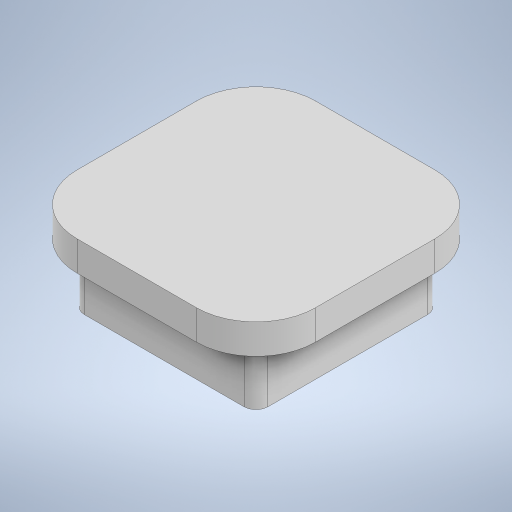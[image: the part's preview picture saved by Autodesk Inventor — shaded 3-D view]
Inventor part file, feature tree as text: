
AUTODESK INVENTOR PART (.ipt)
format: ipt  version: 2023 (Build 270158000, 158)  size: 2,161,664 bytes
history: native  units: in
note: dims shown in document units (in); Inventor stores cm internally (conversion verified against a paired STEP export)
features: extrude x8, other x7, plane x4, sketch x4, projected_geometry x3, fillet x2, chamfer x1
ambient origin geometry x8: Origin, YZ Plane, XZ Plane, XY Plane, X Axis, Y Axis, Z Axis, Center Point
bodies: Solid1 (feature_tree), Solid7 (feature_tree), Solid8 (feature_tree), Solid9 (feature_tree), Solid10 (feature_tree)
feature tree (29):
  plane  "Work Plane1"
  sketch  "Sketch3"  dims[d11=0.0118in d15=0.1969in d16=0.0in]
  extrude  "Extrusion3"  Depth=0.1969in TaperAngle=0.0deg
  extrude  "Extrusion5"  Depth=1.5748in
  extrude  "Extrusion6"  Depth=0.3937in TaperAngle=0.0deg
  plane  "Work Plane2"
  sketch  "Sketch4"  dims[d19=0.1417in d20=0.0in d21=1.5748in]
  extrude  "Extrusion7"  Depth=0.0197in TaperAngle=0.0deg
  extrude  "Extrusion8"  Depth=0.3937in TaperAngle=0.0deg
  plane  "Work Plane3"
  extrude  "Extrusion9"  Depth=0.0197in
  plane  "Work Plane4"
  extrude  "Extrusion10"  Depth=0.0197in
  fillet  "Fillet1"  [1 undecoded]
  chamfer  "Chamfer2"  Distance=0.0059in
  extrude  "Extrusion11"  Depth=0.0039in
  fillet  "Fillet2"  Radius=0.0039in
  projected_geometry  "Projected Loop3"
  other  "lid"
  projected_geometry  "Projected Loop4"
  projected_geometry  "Projected Loop5"
  other  "bottom"
  sketch  "Sketch7"  dims[d22=1.5748in d34=0.3937in d35=0.0in]
  sketch  "Sketch8"  dims[d36=-2.4737in d37=0.9843in d38=0.0in d48=0.3937in d49=0.0in d50=0.0059in d51=0.0059in d52=0.0in d53=0.0059in d55=0.0039in d57=0.0039in d58=0.0079in d59=0.0039in d60=0.0059in d61=0.6201in d62=0.0in d63=0.0in d64=30.0deg d66=0.4434in d67=0.7842in d68=0.0in d69=0.0in d70=0.3937in d71=0.0184in d72=0.0787in d73=45.0deg d74=0.1811in d75=0.1811in d76=0.1811in d77=0.1811in d78=0.1063in d79=0.0098in d80=0.0098in d81=0.0098in d82=0.0098in d83=0.1378in d84=0.248in d85=0.0in d86=0.0787in d17=0.0197in d18=0.0344in]
  other  "MX-solid1-F1"
  other  "MX-solid6-F6"
  other  "T-2-solid1"
  other  "T-2-solid2"
  other  "Boss-Extrude1"
note: 1 required parameter value undecoded (feature->parameter linkage not recoverable at this tier; creation-order binding heuristic only, values carry confidence <= 0.55)
